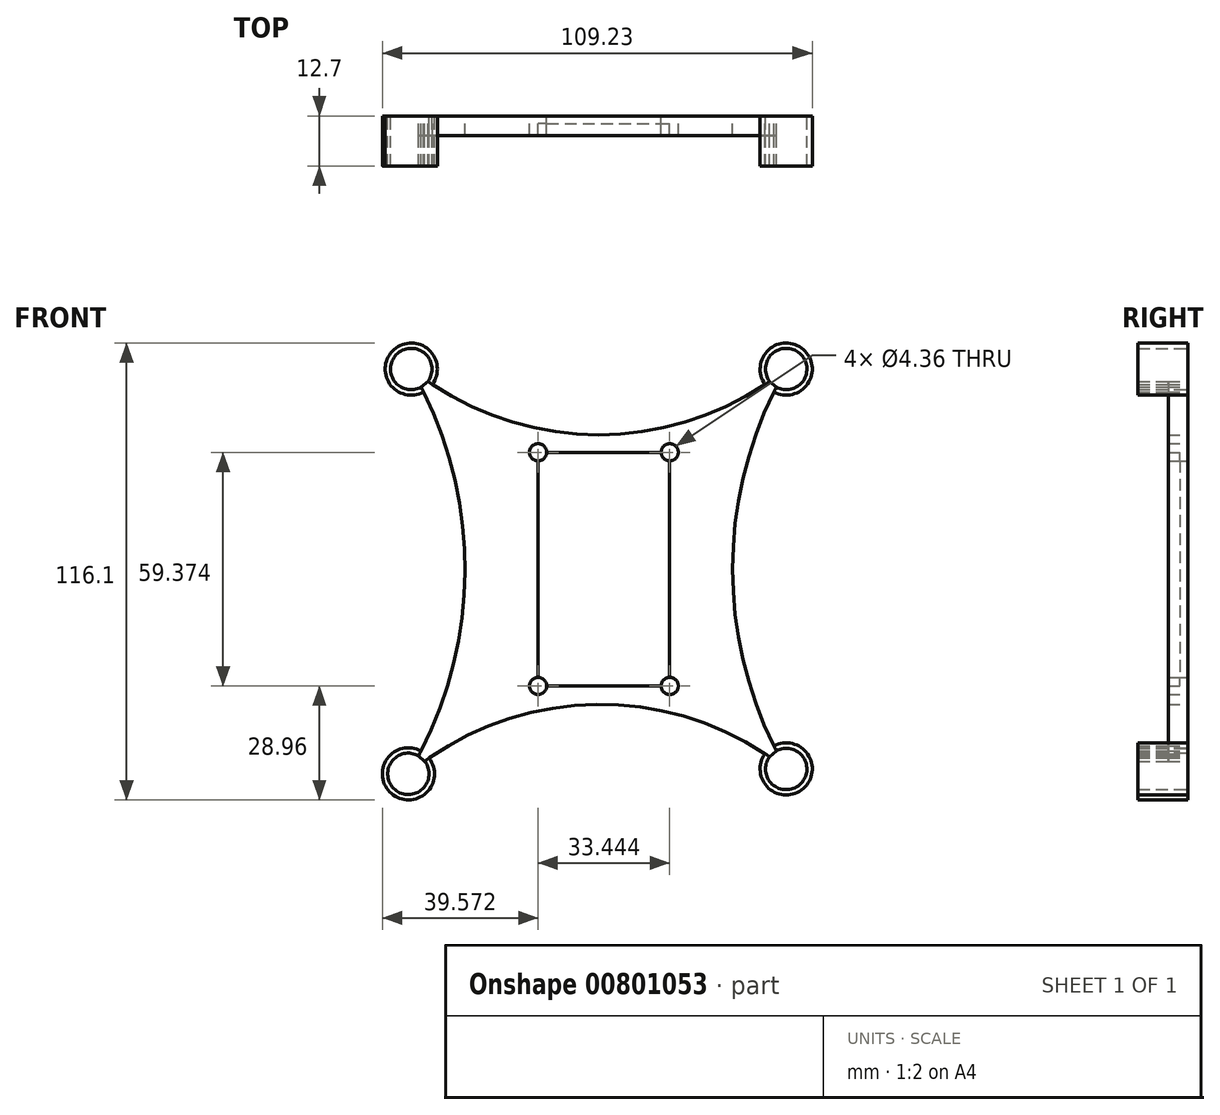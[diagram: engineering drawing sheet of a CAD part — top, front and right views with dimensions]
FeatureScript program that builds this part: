
annotation { "Feature Type Name" : "Feature", "Feature Type Description" : "" }
export const myFeature = defineFeature(function(context is Context, id is Id, definition is map)
    precondition{}
    {
        {
            var Q0;
            Q0=qCreatedBy(makeId("Front.planeOp"),FACE);
            var sketch = newSketch(context, id + "F0", { "sketchPlane" : qUnion([Q0])});
            skArc(sketch, "E0", {"start": v(42.3, 45.72) * mm, "mid": v(31.2, -0.45) * mm, "end": v(42.3, -46.63) * mm});
            skArc(sketch, "E1", {"start": v(-48.6, -47.92) * mm, "mid": v(-36.83, -1.18) * mm, "end": v(-47.93, 45.72) * mm});
            skArc(sketch, "E2", {"start": v(40.57, -48.14) * mm, "mid": v(-3.4, -34.87) * mm, "end": v(-47.02, -49.28) * mm});
            skArc(sketch, "E3", {"start": v(-46.23, 47.2) * mm, "mid": v(-2.82, 33.63) * mm, "end": v(40.6, 47.2) * mm});
            skArc(sketch, "E4", {"start": v(42.3, 45.72) * mm, "mid": v(48.25, 54.32) * mm, "end": v(40.6, 47.2) * mm});
            skArc(sketch, "E5", {"start": v(-46.23, 47.2) * mm, "mid": v(-53.89, 54.32) * mm, "end": v(-47.93, 45.72) * mm});
            skArc(sketch, "E6", {"start": v(-48.6, -47.92) * mm, "mid": v(-54.61, -56.49) * mm, "end": v(-47.02, -49.28) * mm});
            skArc(sketch, "E7", {"start": v(40.57, -48.14) * mm, "mid": v(48.26, -55.22) * mm, "end": v(42.3, -46.63) * mm});
            skArc(sketch, "E8", {"start": v(-46.23, 47.2) * mm, "mid": v(-2.82, 29.5) * mm, "end": v(40.6, 47.2) * mm});
            skArc(sketch, "E9", {"start": v(42.3, 45.72) * mm, "mid": v(25.84, -0.45) * mm, "end": v(42.3, -46.63) * mm});
            skArc(sketch, "E10", {"start": v(40.57, -48.14) * mm, "mid": v(-3.46, -30.42) * mm, "end": v(-47.02, -49.28) * mm});
            skArc(sketch, "E11", {"start": v(-48.6, -47.92) * mm, "mid": v(-31.75, -1.22) * mm, "end": v(-47.93, 45.72) * mm});
            skArc(sketch, "E12", {"start": v(41.68, 44.5) * mm, "mid": v(49.15, 55.35) * mm, "end": v(39.46, 46.43) * mm});
            skArc(sketch, "E13", {"start": v(-45.1, 46.43) * mm, "mid": v(-54.79, 55.35) * mm, "end": v(-47.32, 44.5) * mm});
            skArc(sketch, "E14", {"start": v(-47.97, -46.7) * mm, "mid": v(-55.5, -57.52) * mm, "end": v(-45.9, -48.49) * mm});
            skArc(sketch, "E15", {"start": v(39.43, -47.38) * mm, "mid": v(49.17, -56.24) * mm, "end": v(41.68, -45.41) * mm});
            skLineSegment(sketch, "E16.bottom", {"start": v(-16.05, 29.2) * mm, "end": v(13.04, 29.2) * mm});
            skLineSegment(sketch, "E16.top", {"start": v(-16.05, -30.17) * mm, "end": v(13.04, -30.17) * mm});
            skLineSegment(sketch, "E16.left", {"start": v(-18.23, 27.03) * mm, "end": v(-18.23, -28) * mm});
            skLineSegment(sketch, "E16.right", {"start": v(15.22, 27.03) * mm, "end": v(15.22, -28) * mm});
            skCircle(sketch, "E17", {"center": v(15.22, 29.2) * mm, "radius": 2.18 * mm});
            skCircle(sketch, "E18", {"center": v(-18.23, 29.2) * mm, "radius": 2.18 * mm});
            skCircle(sketch, "E19", {"center": v(15.22, -30.17) * mm, "radius": 2.18 * mm});
            skCircle(sketch, "E20", {"center": v(-18.23, -30.17) * mm, "radius": 2.18 * mm});
            skLineSegment(sketch, "E21", {"start": v(-46.23, 47.2) * mm, "end": v(-47.93, 45.72) * mm});
            skLineSegment(sketch, "E22", {"start": v(40.6, 47.2) * mm, "end": v(42.3, 45.72) * mm});
            skLineSegment(sketch, "E23", {"start": v(42.3, -46.63) * mm, "end": v(40.57, -48.14) * mm});
            skLineSegment(sketch, "E24", {"start": v(-47.02, -49.28) * mm, "end": v(-48.6, -47.92) * mm});
            skSolve(sketch);
        }
        {
            var Q0;
            {var subQ1=sQuery(id+"F0.wireOp",EDGE,"E2");var subQ5=makeQuery(id+"F0.imprint","INTERSECT",VERTEX,{"derivedFrom":[subQ1,sQuery(id+"F0.wireOp",EDGE,"E14")]});Q0=makeQuery(id+"F0.imprint","IMPRINT",FACE,{"disambiguationData":[TD([[makeQuery(id+"F0.imprint","IMPRINT",EDGE,{"disambiguationData":[TD([[subQ5,1.0]])],"derivedFrom":subQ1}),-1.0]])]});}
            var Q1;
            {var subQ0=sQuery(id+"F0.wireOp",EDGE,"E11");Q1=makeQuery(id+"F0.imprint","IMPRINT",FACE,{"disambiguationData":[TD([[makeQuery(id+"F0.imprint","IMPRINT",EDGE,{"derivedFrom":subQ0}),1.0]])]});}
            var Q2;
            {var subQ1=sQuery(id+"F0.wireOp",EDGE,"E3");var subQ5=makeQuery(id+"F0.imprint","INTERSECT",VERTEX,{"derivedFrom":[subQ1,sQuery(id+"F0.wireOp",EDGE,"E12")]});Q2=makeQuery(id+"F0.imprint","IMPRINT",FACE,{"disambiguationData":[TD([[makeQuery(id+"F0.imprint","IMPRINT",EDGE,{"disambiguationData":[TD([[subQ5,1.0]])],"derivedFrom":subQ1}),-1.0]])]});}
            var Q3;
            {var subQ0=sQuery(id+"F0.wireOp",EDGE,"E9");Q3=makeQuery(id+"F0.imprint","IMPRINT",FACE,{"disambiguationData":[TD([[makeQuery(id+"F0.imprint","IMPRINT",EDGE,{"derivedFrom":subQ0}),1.0]])]});}
            var Q4;
            Q4=makeQuery(id+"F0.imprint","IMPRINT",FACE,{"disambiguationData":[TD([[makeQuery(id+"F0.imprint","IMPRINT",EDGE,{"derivedFrom":sQuery(id+"F0.wireOp",EDGE,"E11")}),-1.0]])]});
            var Q5;
            Q5=makeQuery(id+"F0.imprint","IMPRINT",FACE,{"disambiguationData":[TD([[makeQuery(id+"F0.imprint","IMPRINT",EDGE,{"derivedFrom":sQuery(id+"F0.wireOp",EDGE,"E9")}),-1.0]])]});
            extrude(context, id + "F1", {"entities" : qUnion([Q0, Q1, Q2, Q3, Q4, Q5]), "depth" : 5 * mm, "offsetDistance" : 25.4 * mm});
        }
        {
            var Q0;
            {var subQ1=sQuery(id+"F0.wireOp",EDGE,"E5");Q0=makeQuery(id+"F0.imprint","IMPRINT",FACE,{"disambiguationData":[TD([[makeQuery(id+"F0.imprint","IMPRINT",EDGE,{"derivedFrom":subQ1}),-1.0]])]});}
            var Q1;
            {var subQ1=sQuery(id+"F0.wireOp",EDGE,"E4");Q1=makeQuery(id+"F0.imprint","IMPRINT",FACE,{"disambiguationData":[TD([[makeQuery(id+"F0.imprint","IMPRINT",EDGE,{"derivedFrom":subQ1}),-1.0]])]});}
            var Q2;
            {var subQ1=sQuery(id+"F0.wireOp",EDGE,"E7");Q2=makeQuery(id+"F0.imprint","IMPRINT",FACE,{"disambiguationData":[TD([[makeQuery(id+"F0.imprint","IMPRINT",EDGE,{"derivedFrom":subQ1}),-1.0]])]});}
            var Q3;
            {var subQ1=sQuery(id+"F0.wireOp",EDGE,"E6");Q3=makeQuery(id+"F0.imprint","IMPRINT",FACE,{"disambiguationData":[TD([[makeQuery(id+"F0.imprint","IMPRINT",EDGE,{"derivedFrom":subQ1}),-1.0]])]});}
            extrude(context, id + "F2", {"entities" : qUnion([Q0, Q1, Q2, Q3]), "operationType" : NewBodyOperationType.ADD, "depth" : 12.7 * mm, "offsetDistance" : 25.4 * mm});
        }
        {
            var Q0;
            {var subQ3=sQuery(id+"F0.wireOp",EDGE,"E16.bottom");Q0=makeQuery(id+"F0.imprint","IMPRINT",FACE,{"disambiguationData":[TD([[makeQuery(id+"F0.imprint","IMPRINT",EDGE,{"derivedFrom":subQ3}),-1.0]])]});}
            extrude(context, id + "F3", {"entities" : qUnion([Q0]), "operationType" : NewBodyOperationType.ADD, "depth" : 2 * mm, "offsetDistance" : 25.4 * mm});
        }
    });
